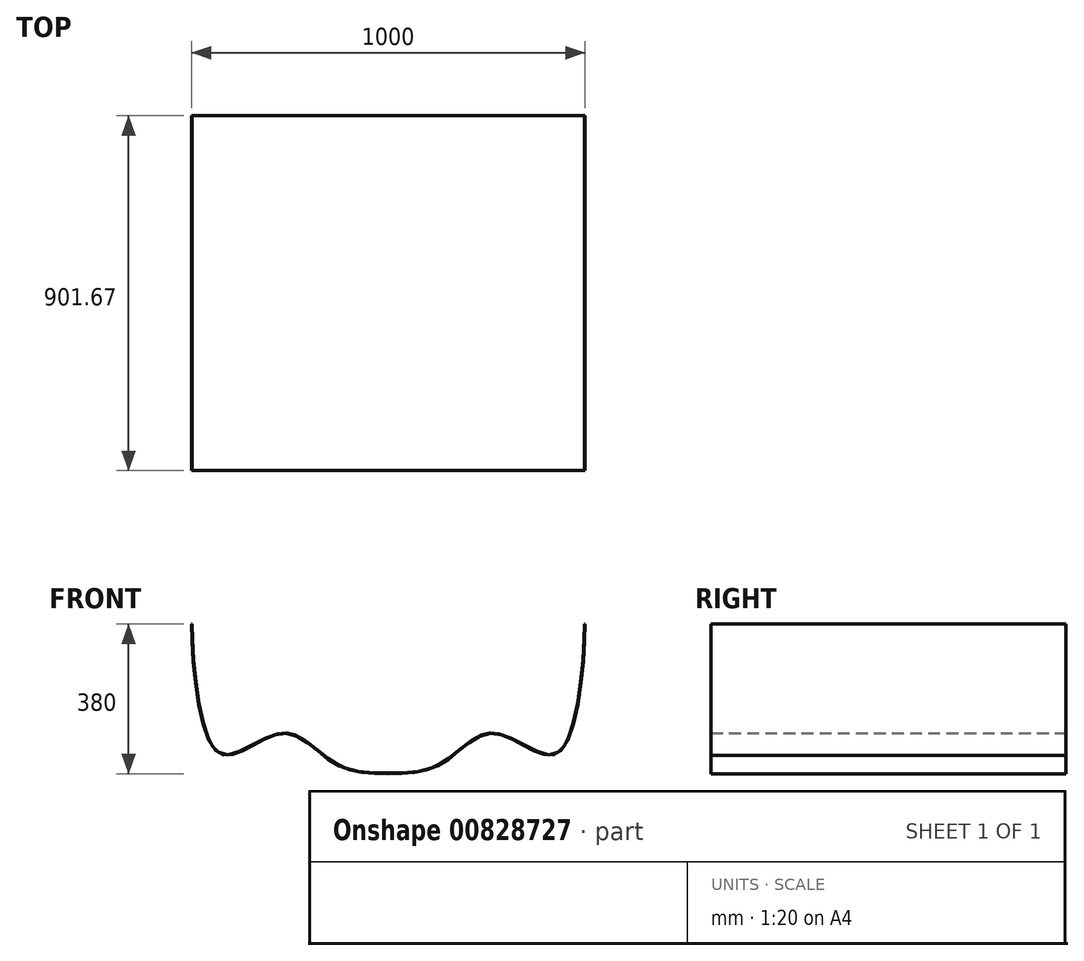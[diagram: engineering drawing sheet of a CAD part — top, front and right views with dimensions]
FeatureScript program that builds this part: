
annotation { "Feature Type Name" : "Feature", "Feature Type Description" : "" }
export const myFeature = defineFeature(function(context is Context, id is Id, definition is map)
    precondition{}
    {
        {
            var Q0;
            Q0=qCreatedBy(makeId("Front.planeOp"),FACE);
            var sketch = newSketch(context, id + "F0", { "sketchPlane" : qUnion([Q0])});
            skLineSegment(sketch, "E0", {"start": v(-489.69, 279.18) * mm, "end": v(510.31, 279.18) * mm, "construction": true});
            skLineSegment(sketch, "E1", {"start": v(10.31, 279.18) * mm, "end": v(10.31, -220.82) * mm, "construction": true});
            skFitSpline(sketch, "E2", {"points": [v(-489.69, 159.18) * mm, v(-434.26, -155.73) * mm, v(-362.81, -163.79) * mm, v(-246, -119.18) * mm, v(-127.07, -193.82) * mm, v(10.31, -220.82) * mm], "startDerivative": vector(0, -863.51) * mm, "endDerivative": vector(833.3, 0) * mm});
            skLineSegment(sketch, "E3", {"start": v(10.31, -220.82) * mm, "end": v(-175.3, -220.82) * mm, "construction": true});
            skFitSpline(sketch, "E4.MirrorCS", {"points": [v(510.31, 159.18) * mm, v(454.88, -155.73) * mm, v(383.44, -163.79) * mm, v(266.62, -119.18) * mm, v(147.7, -193.82) * mm, v(10.31, -220.82) * mm], "startDerivative": vector(0, -863.51) * mm, "endDerivative": vector(-833.3, 0) * mm});
            skFitSpline(sketch, "E5.1", {"points": [v(-488.09, 159.18) * mm, v(-488.09, 150.2) * mm, v(-487.74, 130.08) * mm, v(-486.1, 95) * mm, v(-483.28, 56.67) * mm, v(-479.2, 16.72) * mm, v(-473.78, -23.22) * mm, v(-466.97, -61.5) * mm, v(-460.07, -90.66) * mm, v(-453.79, -111.52) * mm, v(-448.69, -125.72) * mm, v(-444.12, -136.17) * mm, v(-440.27, -143.6) * mm, v(-437.29, -148.68) * mm, v(-434.21, -153.24) * mm, v(-431.05, -157.24) * mm, v(-427.8, -160.72) * mm, v(-423.36, -164.67) * mm, v(-417.6, -168.4) * mm, v(-410.34, -171.15) * mm, v(-402.73, -172.36) * mm, v(-392.07, -172.12) * mm, v(-380.66, -169.37) * mm, v(-368.65, -164.73) * mm, v(-356.27, -159.05) * mm, v(-340.2, -150.45) * mm, v(-320.21, -139.28) * mm, v(-303.2, -130.58) * mm, v(-289.48, -124.77) * mm, v(-279.16, -121.18) * mm, v(-268.84, -118.57) * mm, v(-260.26, -117.38) * mm, v(-253.42, -117.12) * mm, v(-248.3, -117.3) * mm, v(-243.22, -117.88) * mm, v(-238.18, -118.86) * mm, v(-233.17, -120.21) * mm, v(-226.56, -122.47) * mm, v(-218.38, -126.09) * mm, v(-208.68, -131.49) * mm, v(-195.87, -139.82) * mm, v(-180.02, -151.87) * mm, v(-164.23, -164.79) * mm, v(-151.54, -174.84) * mm, v(-141.98, -182.05) * mm, v(-133.97, -187.62) * mm, v(-127.52, -191.7) * mm, v(-122.66, -194.57) * mm, v(-117.78, -197.22) * mm, v(-111.22, -200.5) * mm, v(-102.92, -204.13) * mm, v(-92.8, -207.8) * mm, v(-79.04, -211.84) * mm, v(-61.27, -215.45) * mm, v(-38.86, -217.95) * mm, v(-15.15, -219.08) * mm, v(1.64, -219.22) * mm, v(10.31, -219.22) * mm]});
            skFitSpline(sketch, "E5.2", {"points": [v(508.71, 159.18) * mm, v(508.71, 150.2) * mm, v(508.36, 130.08) * mm, v(506.73, 95) * mm, v(503.9, 56.67) * mm, v(499.82, 16.72) * mm, v(494.4, -23.22) * mm, v(487.6, -61.5) * mm, v(480.7, -90.66) * mm, v(474.4, -111.52) * mm, v(469.31, -125.72) * mm, v(464.74, -136.17) * mm, v(460.9, -143.6) * mm, v(457.9, -148.68) * mm, v(454.84, -153.24) * mm, v(451.68, -157.24) * mm, v(448.43, -160.72) * mm, v(443.98, -164.67) * mm, v(438.22, -168.4) * mm, v(430.97, -171.15) * mm, v(423.35, -172.36) * mm, v(412.69, -172.12) * mm, v(401.29, -169.37) * mm, v(389.27, -164.73) * mm, v(376.9, -159.05) * mm, v(360.82, -150.45) * mm, v(340.84, -139.28) * mm, v(323.82, -130.58) * mm, v(310.1, -124.77) * mm, v(299.79, -121.18) * mm, v(289.46, -118.57) * mm, v(280.88, -117.38) * mm, v(274.04, -117.12) * mm, v(268.93, -117.3) * mm, v(263.84, -117.88) * mm, v(258.8, -118.86) * mm, v(253.8, -120.21) * mm, v(247.18, -122.47) * mm, v(239, -126.09) * mm, v(229.3, -131.49) * mm, v(216.5, -139.82) * mm, v(200.65, -151.87) * mm, v(184.85, -164.79) * mm, v(172.16, -174.84) * mm, v(162.6, -182.05) * mm, v(154.6, -187.62) * mm, v(148.15, -191.7) * mm, v(143.29, -194.57) * mm, v(138.4, -197.22) * mm, v(131.84, -200.5) * mm, v(123.55, -204.13) * mm, v(113.42, -207.8) * mm, v(99.66, -211.84) * mm, v(81.9, -215.45) * mm, v(59.48, -217.95) * mm, v(35.77, -219.08) * mm, v(18.98, -219.22) * mm, v(10.31, -219.22) * mm]});
            skLineSegment(sketch, "E6", {"start": v(508.71, 159.18) * mm, "end": v(510.31, 159.18) * mm});
            skLineSegment(sketch, "E7", {"start": v(-489.69, 159.18) * mm, "end": v(-488.09, 159.18) * mm});
            skSolve(sketch);
        }
        {
            var Q0;
            Q0=makeQuery(id+"F0.imprint","IMPRINT",FACE,{"disambiguationData":[TD([[makeQuery(id+"F0.imprint","IMPRINT",EDGE,{"derivedFrom":sQuery(id+"F0.wireOp",EDGE,"E2")}),1.0]])]});
            extrude(context, id + "F1", {"entities" : qUnion([Q0]), "depth" : 901.67 * mm, "offsetDistance" : 25 * mm});
        }
    });
